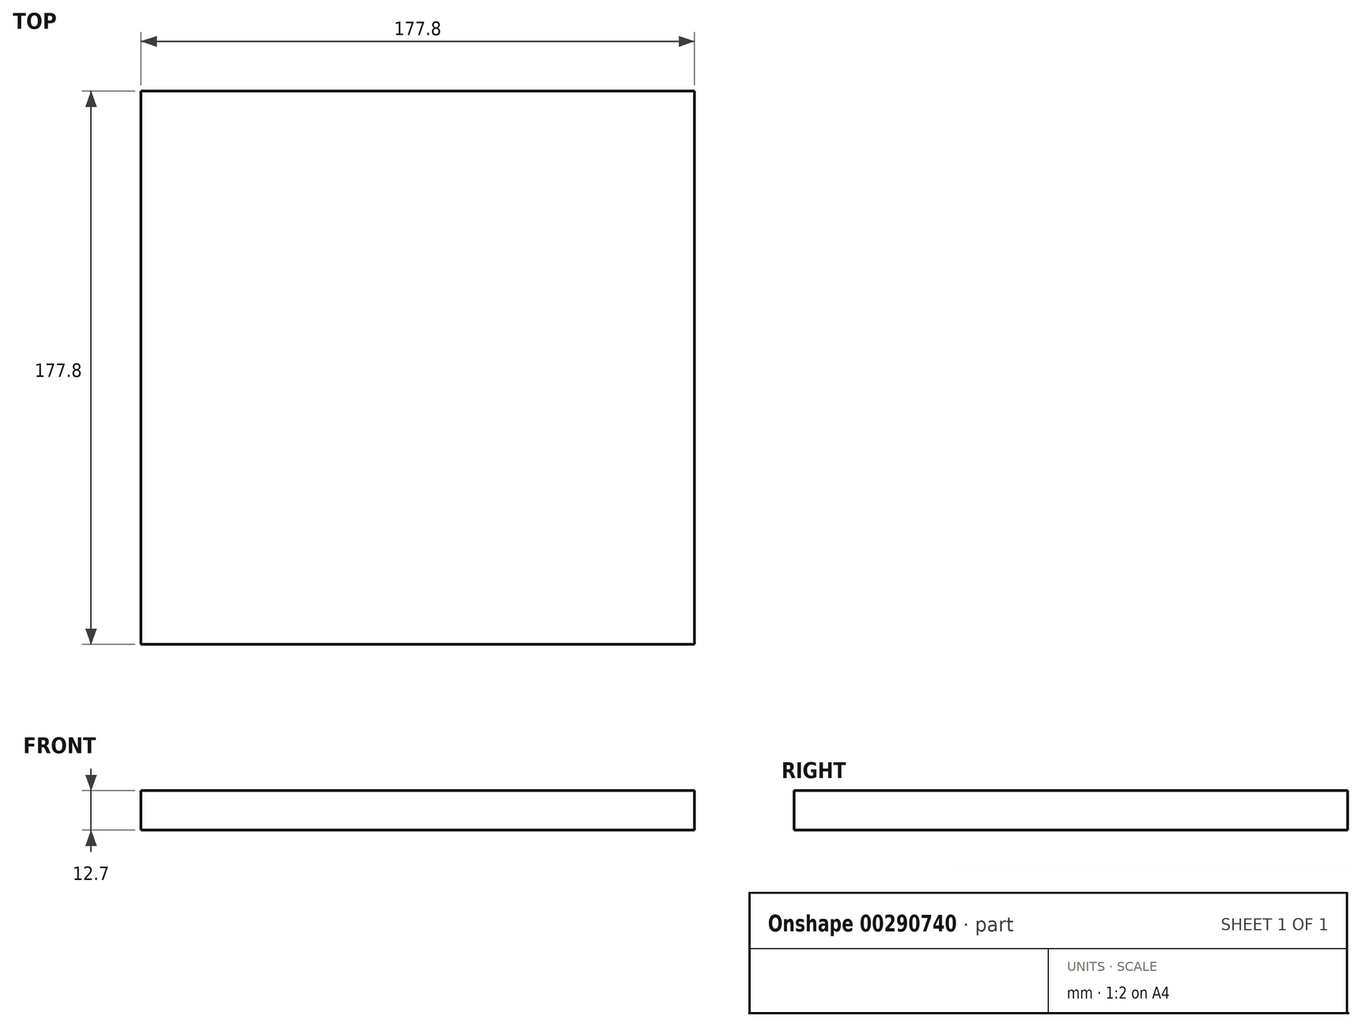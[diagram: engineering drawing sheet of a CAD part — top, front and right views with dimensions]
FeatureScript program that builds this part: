
annotation { "Feature Type Name" : "Feature", "Feature Type Description" : "" }
export const myFeature = defineFeature(function(context is Context, id is Id, definition is map)
    precondition{}
    {
        {
            var Q0;
            Q0=qCreatedBy(makeId("Top.planeOp"),FACE);
            var sketch = newSketch(context, id + "F0", { "sketchPlane" : qUnion([Q0])});
            skLineSegment(sketch, "E0.bottom", {"start": v(0, 0) * mm, "end": v(177.8, 0) * mm});
            skLineSegment(sketch, "E0.top", {"start": v(0, 177.8) * mm, "end": v(177.8, 177.8) * mm});
            skLineSegment(sketch, "E0.left", {"start": v(0, 0) * mm, "end": v(0, 177.8) * mm});
            skLineSegment(sketch, "E0.right", {"start": v(177.8, 0) * mm, "end": v(177.8, 177.8) * mm});
            skSolve(sketch);
        }
        {
            var Q0;
            Q0 = qSketchRegion(id + "F0", true);
            extrude(context, id + "F1", {"entities" : qUnion([Q0]), "depth" : 12.7 * mm});
        }
    });
